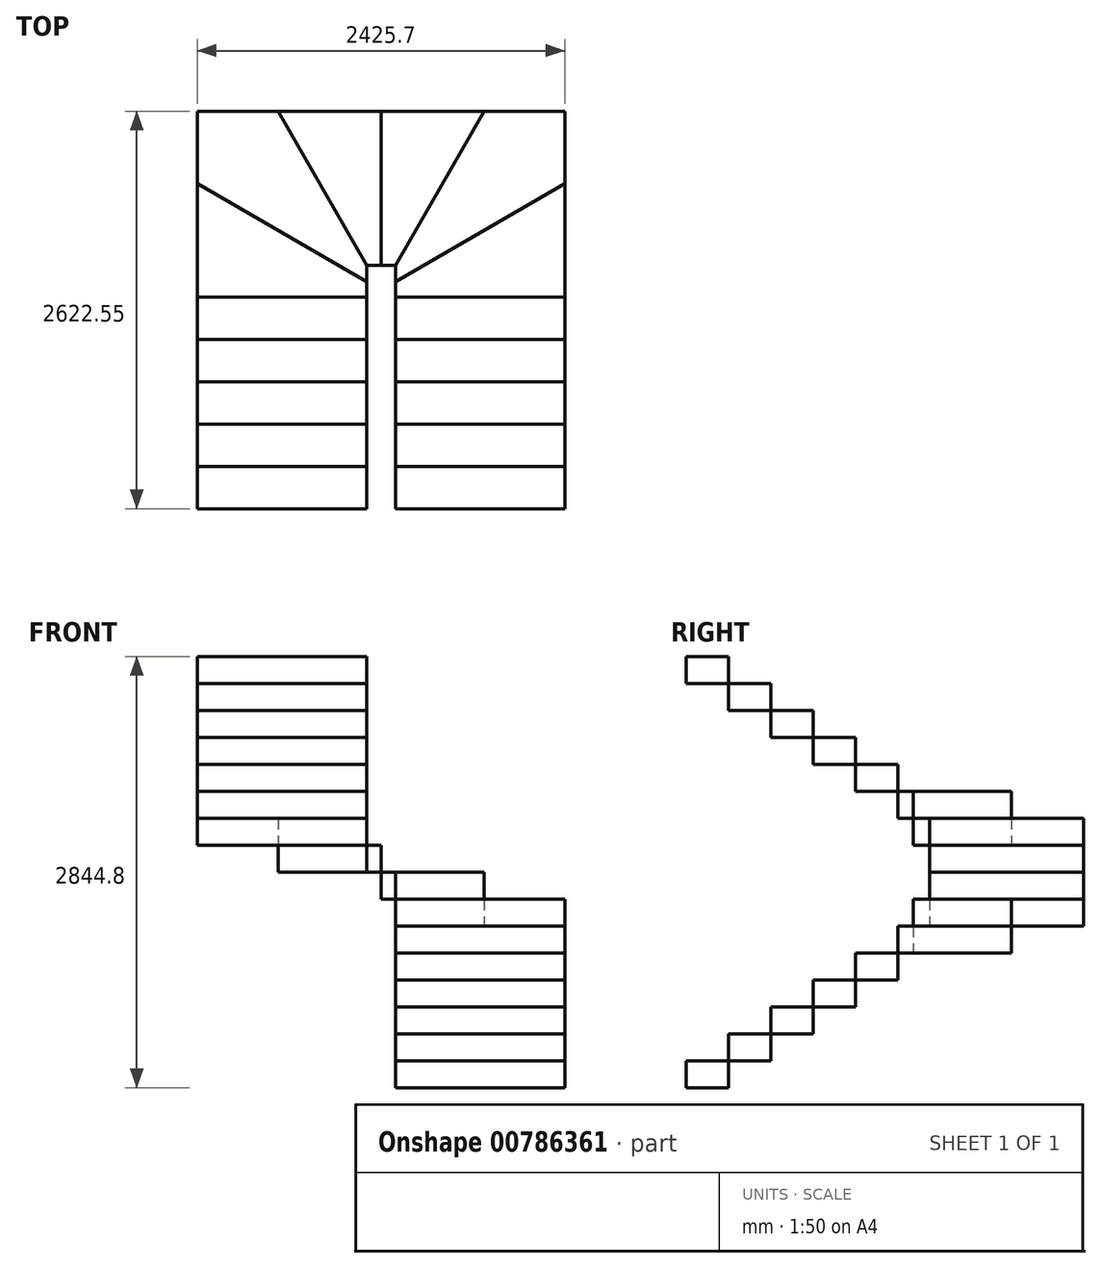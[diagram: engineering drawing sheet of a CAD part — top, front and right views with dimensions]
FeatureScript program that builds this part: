
annotation { "Feature Type Name" : "Feature", "Feature Type Description" : "" }
export const myFeature = defineFeature(function(context is Context, id is Id, definition is map)
    precondition{}
    {
        {
            var Q0;
            Q0=qCreatedBy(makeId("Top.planeOp"),FACE);
            var sketch = newSketch(context, id + "F0", { "sketchPlane" : qUnion([Q0])});
            skCircle(sketch, "E0", {"center": v(0, 0) * mm, "radius": 1212.85 * mm, "construction": true});
            skLineSegment(sketch, "E1", {"start": v(0, 0) * mm, "end": v(-1212.85, 0) * mm, "construction": true});
            skLineSegment(sketch, "E2", {"start": v(0, 0) * mm, "end": v(1212.85, 0) * mm, "construction": true});
            skLineSegment(sketch, "E3", {"start": v(0, 0) * mm, "end": v(0, 1212.85) * mm, "construction": true});
            skLineSegment(sketch, "E4.bottom", {"start": v(95.25, 1323.25) * mm, "end": v(-95.25, 1323.25) * mm, "construction": true});
            skLineSegment(sketch, "E4.top", {"start": v(95.25, -3517.78) * mm, "end": v(-95.25, -3517.78) * mm, "construction": true});
            skLineSegment(sketch, "E4.left", {"start": v(95.25, 1323.25) * mm, "end": v(95.25, -3517.78) * mm, "construction": true});
            skLineSegment(sketch, "E4.right", {"start": v(-95.25, 1323.25) * mm, "end": v(-95.25, -3517.78) * mm, "construction": true});
            skLineSegment(sketch, "E5", {"start": v(-190.5, 1323.25) * mm, "end": v(-190.5, -3534.77) * mm, "construction": true});
            skLineSegment(sketch, "E6.bottom", {"start": v(-95.25, 0) * mm, "end": v(-1212.85, 0) * mm});
            skLineSegment(sketch, "E6.top", {"start": v(-95.25, -279.4) * mm, "end": v(-1212.85, -279.4) * mm});
            skLineSegment(sketch, "E6.left", {"start": v(-95.25, 0) * mm, "end": v(-95.25, -279.4) * mm});
            skLineSegment(sketch, "E6.right", {"start": v(-1212.85, 0) * mm, "end": v(-1212.85, -279.4) * mm});
            skLineSegment(sketch, "E7", {"start": v(-1212.85, 742.65) * mm, "end": v(73.46, 0) * mm, "construction": true});
            skLineSegment(sketch, "E8", {"start": v(-740.5, 1323.25) * mm, "end": v(623.95, -1040.04) * mm, "construction": true});
            skPoint(sketch, "E9", {"position": v(-190.5, 152.4) * mm});
            skPoint(sketch, "E10", {"position": v(-153.9, 307.25) * mm});
            skLineSegment(sketch, "E11", {"start": v(-153.9, 307.25) * mm, "end": v(0, 307.25) * mm, "construction": true});
            skPoint(sketch, "E12", {"position": v(0, 205.65) * mm});
            skLineSegment(sketch, "E13", {"start": v(0, 205.65) * mm, "end": v(-95.25, 205.65) * mm});
            skPoint(sketch, "E14", {"position": v(-95.25, 205.65) * mm});
            skPoint(sketch, "E15", {"position": v(-95.25, 97.4) * mm});
            skLineSegment(sketch, "E16", {"start": v(-95.25, 0) * mm, "end": v(-95.25, 97.4) * mm});
            skLineSegment(sketch, "E17", {"start": v(-1212.85, 742.65) * mm, "end": v(-1212.85, 0) * mm});
            skLineSegment(sketch, "E18", {"start": v(-1212.85, 742.65) * mm, "end": v(-95.25, 97.4) * mm});
            skLineSegment(sketch, "E19", {"start": v(-95.25, 97.4) * mm, "end": v(-95.25, 205.65) * mm});
            skLineSegment(sketch, "E20", {"start": v(0, 205.65) * mm, "end": v(0, 1323.25) * mm});
            skLineSegment(sketch, "E21", {"start": v(0, 1323.25) * mm, "end": v(-1212.85, 1323.25) * mm});
            skPoint(sketch, "E22", {"position": v(-740.5, 1323.25) * mm});
            skLineSegment(sketch, "E23", {"start": v(-95.25, 205.65) * mm, "end": v(-740.5, 1323.25) * mm});
            skLineSegment(sketch, "E24", {"start": v(-1212.85, 1323.25) * mm, "end": v(-1212.85, 742.65) * mm});
            skSolve(sketch);
        }
        {
            var Q0;
            Q0=qCreatedBy(makeId("Top.planeOp"),FACE);
            var sketch = newSketch(context, id + "F1", { "sketchPlane" : qUnion([Q0])});
            skLineSegment(sketch, "E25.bottom", {"start": v(95.25, 0) * mm, "end": v(1212.85, 0) * mm});
            skLineSegment(sketch, "E25.top", {"start": v(95.25, -279.4) * mm, "end": v(1212.85, -279.4) * mm});
            skLineSegment(sketch, "E25.left", {"start": v(95.25, 0) * mm, "end": v(95.25, -279.4) * mm});
            skLineSegment(sketch, "E25.right", {"start": v(1212.85, 0) * mm, "end": v(1212.85, -279.4) * mm});
            skLineSegment(sketch, "E26", {"start": v(95.25, 0) * mm, "end": v(95.25, 101.6) * mm});
            skLineSegment(sketch, "E27", {"start": v(95.25, 101.6) * mm, "end": v(1212.85, 749.3) * mm});
            skLineSegment(sketch, "E28", {"start": v(1212.85, 749.3) * mm, "end": v(1212.85, 0) * mm});
            skLineSegment(sketch, "E29", {"start": v(190.5, 0) * mm, "end": v(190.5, 156.8) * mm, "construction": true});
            skLineSegment(sketch, "E30", {"start": v(0, 209.55) * mm, "end": v(95.25, 209.55) * mm});
            skLineSegment(sketch, "E31", {"start": v(95.25, 209.55) * mm, "end": v(679.45, 1225.55) * mm});
            skLineSegment(sketch, "E32", {"start": v(679.45, 1225.55) * mm, "end": v(0, 1225.55) * mm});
            skLineSegment(sketch, "E33", {"start": v(0, 1225.55) * mm, "end": v(0, 209.55) * mm});
            skLineSegment(sketch, "E34", {"start": v(679.45, 1225.55) * mm, "end": v(1212.85, 1225.55) * mm});
            skLineSegment(sketch, "E35", {"start": v(1212.85, 1225.55) * mm, "end": v(1212.85, 749.3) * mm});
            skLineSegment(sketch, "E36", {"start": v(0, 304.8) * mm, "end": v(150.02, 304.8) * mm, "construction": true});
            skLineSegment(sketch, "E37", {"start": v(95.25, 209.55) * mm, "end": v(95.25, 101.6) * mm});
            skLineSegment(sketch, "E38", {"start": v(150.02, 304.8) * mm, "end": v(190.5, 304.8) * mm, "construction": true});
            skLineSegment(sketch, "E39", {"start": v(190.5, 304.8) * mm, "end": v(190.5, 156.8) * mm, "construction": true});
            skLineSegment(sketch, "E40", {"start": v(95.25, -279.4) * mm, "end": v(95.25, -558.8) * mm});
            skLineSegment(sketch, "E41", {"start": v(95.25, -558.8) * mm, "end": v(1212.85, -558.8) * mm});
            skLineSegment(sketch, "E42", {"start": v(1212.85, -558.8) * mm, "end": v(1212.85, -279.4) * mm});
            skLineSegment(sketch, "E43", {"start": v(95.25, -558.8) * mm, "end": v(95.25, -838.2) * mm});
            skLineSegment(sketch, "E44", {"start": v(95.25, -838.2) * mm, "end": v(1212.85, -838.2) * mm});
            skLineSegment(sketch, "E45", {"start": v(1212.85, -838.2) * mm, "end": v(1212.85, -558.8) * mm});
            skLineSegment(sketch, "E46", {"start": v(95.25, -838.2) * mm, "end": v(95.25, -1117.6) * mm});
            skLineSegment(sketch, "E47", {"start": v(95.25, -1117.6) * mm, "end": v(1212.85, -1117.6) * mm});
            skLineSegment(sketch, "E48", {"start": v(1212.85, -1117.6) * mm, "end": v(1212.85, -838.2) * mm});
            skLineSegment(sketch, "E49", {"start": v(95.25, -1117.6) * mm, "end": v(95.25, -1397) * mm});
            skLineSegment(sketch, "E50", {"start": v(95.25, -1397) * mm, "end": v(1212.85, -1397) * mm});
            skLineSegment(sketch, "E51", {"start": v(1212.85, -1397) * mm, "end": v(1212.85, -1117.6) * mm});
            skSolve(sketch);
        }
        {
            var Q0;
            Q0=qCreatedBy(makeId("Top.planeOp"),FACE);
            var sketch = newSketch(context, id + "F2", { "sketchPlane" : qUnion([Q0])});
            skLineSegment(sketch, "E52", {"start": v(0, 209.55) * mm, "end": v(-95.25, 209.55) * mm});
            skLineSegment(sketch, "E53", {"start": v(-95.25, 209.55) * mm, "end": v(-679.45, 1225.55) * mm});
            skLineSegment(sketch, "E54", {"start": v(-679.45, 1225.55) * mm, "end": v(0, 1225.55) * mm});
            skLineSegment(sketch, "E55", {"start": v(0, 1225.55) * mm, "end": v(0, 209.55) * mm});
            skLineSegment(sketch, "E56", {"start": v(-679.45, 1225.55) * mm, "end": v(-1212.85, 1225.55) * mm});
            skLineSegment(sketch, "E57", {"start": v(-1212.85, 1225.55) * mm, "end": v(-1212.85, 749.3) * mm});
            skLineSegment(sketch, "E58", {"start": v(-1212.85, 749.3) * mm, "end": v(-95.25, 101.6) * mm});
            skLineSegment(sketch, "E59", {"start": v(-95.25, 101.6) * mm, "end": v(-95.25, 209.55) * mm});
            skLineSegment(sketch, "E60", {"start": v(-95.25, 101.6) * mm, "end": v(-95.25, 0) * mm});
            skLineSegment(sketch, "E61", {"start": v(-95.25, 0) * mm, "end": v(-1212.85, 0) * mm});
            skLineSegment(sketch, "E62", {"start": v(-1212.85, 0) * mm, "end": v(-1212.85, 749.3) * mm});
            skLineSegment(sketch, "E63", {"start": v(-1212.85, 0) * mm, "end": v(-1212.85, -1397) * mm});
            skLineSegment(sketch, "E64", {"start": v(-1212.85, -1397) * mm, "end": v(-95.25, -1397) * mm});
            skLineSegment(sketch, "E65", {"start": v(-95.25, -1397) * mm, "end": v(-95.25, 0) * mm});
            skLineSegment(sketch, "E66", {"start": v(-95.25, -279.4) * mm, "end": v(-1212.85, -279.4) * mm});
            skLineSegment(sketch, "E67", {"start": v(-95.25, -558.8) * mm, "end": v(-1212.85, -558.8) * mm});
            skLineSegment(sketch, "E68", {"start": v(-1212.85, -838.2) * mm, "end": v(-95.25, -838.2) * mm});
            skLineSegment(sketch, "E69", {"start": v(-1212.85, -1117.6) * mm, "end": v(-95.25, -1117.6) * mm});
            skSolve(sketch);
        }
        {
            var Q0;
            Q0=makeQuery(id+"F1.imprint","IMPRINT",FACE,{"disambiguationData":[TD([[makeQuery(id+"F1.imprint","IMPRINT",EDGE,{"derivedFrom":sQuery(id+"F1.wireOp",EDGE,"E47")}),-1.0]])]});
            extrude(context, id + "F3", {"entities" : qUnion([Q0]), "depth" : 177.8 * mm, "offsetDistance" : 25.4 * mm});
        }
        {
            var Q0;
            Q0=makeQuery(id+"F1.imprint","IMPRINT",FACE,{"disambiguationData":[TD([[makeQuery(id+"F1.imprint","IMPRINT",EDGE,{"derivedFrom":sQuery(id+"F1.wireOp",EDGE,"E44")}),-1.0]])]});
            extrude(context, id + "F4", {"entities" : qUnion([Q0]), "depth" : 355.6 * mm, "offsetDistance" : 25.4 * mm, "hasSecondDirection" : true, "secondDirectionOppositeDirection" : true, "secondDirectionDepth" : -177.8 * mm});
        }
        {
            var Q0;
            Q0=makeQuery(id+"F1.imprint","IMPRINT",FACE,{"disambiguationData":[TD([[makeQuery(id+"F1.imprint","IMPRINT",EDGE,{"derivedFrom":sQuery(id+"F1.wireOp",EDGE,"E41")}),-1.0]])]});
            extrude(context, id + "F5", {"entities" : qUnion([Q0]), "depth" : 533.4 * mm, "offsetDistance" : 25.4 * mm, "hasSecondDirection" : true, "secondDirectionOppositeDirection" : true, "secondDirectionDepth" : -355.6 * mm});
        }
        {
            var Q0;
            Q0=makeQuery(id+"F1.imprint","IMPRINT",FACE,{"disambiguationData":[TD([[makeQuery(id+"F1.imprint","IMPRINT",EDGE,{"derivedFrom":sQuery(id+"F1.wireOp",EDGE,"E25.top")}),-1.0]])]});
            extrude(context, id + "F6", {"entities" : qUnion([Q0]), "depth" : 711.2 * mm, "offsetDistance" : 25.4 * mm, "hasSecondDirection" : true, "secondDirectionOppositeDirection" : true, "secondDirectionDepth" : -533.4 * mm});
        }
        {
            var Q0;
            Q0=makeQuery(id+"F1.imprint","IMPRINT",FACE,{"disambiguationData":[TD([[makeQuery(id+"F1.imprint","IMPRINT",EDGE,{"derivedFrom":sQuery(id+"F1.wireOp",EDGE,"E25.bottom")}),-1.0]])]});
            extrude(context, id + "F7", {"entities" : qUnion([Q0]), "depth" : 889 * mm, "offsetDistance" : 25.4 * mm, "hasSecondDirection" : true, "secondDirectionOppositeDirection" : true, "secondDirectionDepth" : -711.2 * mm});
        }
        {
            var Q0;
            Q0=makeQuery(id+"F1.imprint","IMPRINT",FACE,{"disambiguationData":[TD([[makeQuery(id+"F1.imprint","IMPRINT",EDGE,{"derivedFrom":sQuery(id+"F1.wireOp",EDGE,"E25.bottom")}),1.0]])]});
            extrude(context, id + "F8", {"entities" : qUnion([Q0]), "depth" : 1066.8 * mm, "offsetDistance" : 25.4 * mm, "hasSecondDirection" : true, "secondDirectionOppositeDirection" : true, "secondDirectionDepth" : -889 * mm});
        }
        {
            var Q0;
            Q0=makeQuery(id+"F1.imprint","IMPRINT",FACE,{"disambiguationData":[TD([[makeQuery(id+"F1.imprint","IMPRINT",EDGE,{"derivedFrom":sQuery(id+"F1.wireOp",EDGE,"E27")}),1.0]])]});
            extrude(context, id + "F9", {"entities" : qUnion([Q0]), "depth" : 1244.6 * mm, "offsetDistance" : 25.4 * mm, "hasSecondDirection" : true, "secondDirectionOppositeDirection" : true, "secondDirectionDepth" : -1066.8 * mm});
        }
        {
            var Q0;
            Q0=makeQuery(id+"F1.imprint","IMPRINT",FACE,{"disambiguationData":[TD([[makeQuery(id+"F1.imprint","IMPRINT",EDGE,{"derivedFrom":sQuery(id+"F1.wireOp",EDGE,"E30")}),1.0]])]});
            extrude(context, id + "F10", {"entities" : qUnion([Q0]), "depth" : 1422.4 * mm, "offsetDistance" : 25.4 * mm, "hasSecondDirection" : true, "secondDirectionOppositeDirection" : true, "secondDirectionDepth" : -1244.6 * mm});
        }
        {
            var Q0;
            Q0=makeQuery(id+"F2.imprint","IMPRINT",FACE,{"disambiguationData":[TD([[makeQuery(id+"F2.imprint","IMPRINT",EDGE,{"derivedFrom":sQuery(id+"F2.wireOp",EDGE,"E52")}),-1.0]])]});
            extrude(context, id + "F11", {"entities" : qUnion([Q0]), "depth" : 1600.2 * mm, "offsetDistance" : 25.4 * mm, "hasSecondDirection" : true, "secondDirectionOppositeDirection" : true, "secondDirectionDepth" : -1422.4 * mm});
        }
        {
            var Q0;
            Q0=makeQuery(id+"F2.imprint","IMPRINT",FACE,{"disambiguationData":[TD([[makeQuery(id+"F2.imprint","IMPRINT",EDGE,{"derivedFrom":sQuery(id+"F2.wireOp",EDGE,"E53")}),1.0]])]});
            extrude(context, id + "F12", {"entities" : qUnion([Q0]), "depth" : 1778 * mm, "offsetDistance" : 25.4 * mm, "hasSecondDirection" : true, "secondDirectionOppositeDirection" : true, "secondDirectionDepth" : -1600.2 * mm});
        }
        {
            var Q0;
            Q0=makeQuery(id+"F2.imprint","IMPRINT",FACE,{"disambiguationData":[TD([[makeQuery(id+"F2.imprint","IMPRINT",EDGE,{"derivedFrom":sQuery(id+"F2.wireOp",EDGE,"E58")}),-1.0]])]});
            extrude(context, id + "F13", {"entities" : qUnion([Q0]), "depth" : 1955.8 * mm, "offsetDistance" : 25.4 * mm, "hasSecondDirection" : true, "secondDirectionOppositeDirection" : true, "secondDirectionDepth" : -1778 * mm});
        }
        {
            var Q0;
            {var subQ0=sQuery(id+"F2.wireOp",EDGE,"E61");Q0=makeQuery(id+"F2.imprint","IMPRINT",FACE,{"disambiguationData":[TD([[makeQuery(id+"F2.imprint","IMPRINT",EDGE,{"derivedFrom":subQ0}),1.0]])]});}
            extrude(context, id + "F14", {"entities" : qUnion([Q0]), "depth" : 2133.6 * mm, "offsetDistance" : 25.4 * mm, "hasSecondDirection" : true, "secondDirectionOppositeDirection" : true, "secondDirectionDepth" : -1955.8 * mm});
        }
        {
            var Q0;
            {var subQ0=sQuery(id+"F2.wireOp",EDGE,"E66");Q0=makeQuery(id+"F2.imprint","IMPRINT",FACE,{"disambiguationData":[TD([[makeQuery(id+"F2.imprint","IMPRINT",EDGE,{"derivedFrom":subQ0}),1.0]])]});}
            extrude(context, id + "F15", {"entities" : qUnion([Q0]), "depth" : 2311.4 * mm, "offsetDistance" : 25.4 * mm, "hasSecondDirection" : true, "secondDirectionOppositeDirection" : true, "secondDirectionDepth" : -2133.6 * mm});
        }
        {
            var Q0;
            {var subQ0=sQuery(id+"F2.wireOp",EDGE,"E67");Q0=makeQuery(id+"F2.imprint","IMPRINT",FACE,{"disambiguationData":[TD([[makeQuery(id+"F2.imprint","IMPRINT",EDGE,{"derivedFrom":subQ0}),1.0]])]});}
            extrude(context, id + "F16", {"entities" : qUnion([Q0]), "depth" : 2489.2 * mm, "offsetDistance" : 25.4 * mm, "hasSecondDirection" : true, "secondDirectionOppositeDirection" : true, "secondDirectionDepth" : -2311.4 * mm});
        }
        {
            var Q0;
            {var subQ0=sQuery(id+"F2.wireOp",EDGE,"E68");Q0=makeQuery(id+"F2.imprint","IMPRINT",FACE,{"disambiguationData":[TD([[makeQuery(id+"F2.imprint","IMPRINT",EDGE,{"derivedFrom":subQ0}),-1.0]])]});}
            extrude(context, id + "F17", {"entities" : qUnion([Q0]), "operationType" : NewBodyOperationType.ADD, "depth" : 2667 * mm, "offsetDistance" : 25.4 * mm, "hasSecondDirection" : true, "secondDirectionOppositeDirection" : true, "secondDirectionDepth" : -2489.2 * mm});
        }
        {
            var Q0;
            {var subQ0=sQuery(id+"F2.wireOp",EDGE,"E64");Q0=makeQuery(id+"F2.imprint","IMPRINT",FACE,{"disambiguationData":[TD([[makeQuery(id+"F2.imprint","IMPRINT",EDGE,{"derivedFrom":subQ0}),1.0]])]});}
            extrude(context, id + "F18", {"entities" : qUnion([Q0]), "depth" : 2844.8 * mm, "offsetDistance" : 25.4 * mm, "hasSecondDirection" : true, "secondDirectionOppositeDirection" : true, "secondDirectionDepth" : -2667 * mm});
        }
    });
